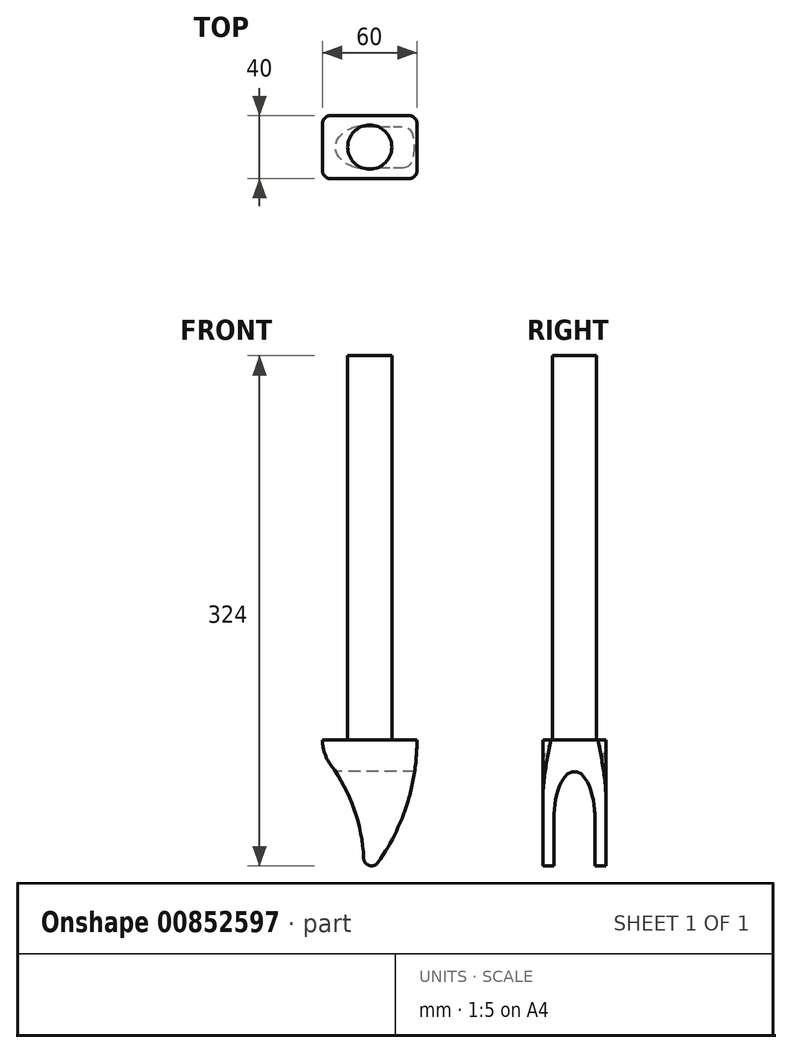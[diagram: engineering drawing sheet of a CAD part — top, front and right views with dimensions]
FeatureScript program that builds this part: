
annotation { "Feature Type Name" : "Feature", "Feature Type Description" : "" }
export const myFeature = defineFeature(function(context is Context, id is Id, definition is map)
    precondition{}
    {
        {
            var Q0;
            Q0=qCreatedBy(makeId("Top.planeOp"),FACE);
            var sketch = newSketch(context, id + "F0", { "sketchPlane" : qUnion([Q0])});
            skCircle(sketch, "E0", {"center": v(0, 0) * mm, "radius": 14 * mm});
            skSolve(sketch);
        }
        {
            var Q0;
            Q0=makeQuery(id+"F0.imprint","IMPRINT",FACE,{"disambiguationData":[TD([[makeQuery(id+"F0.imprint","IMPRINT",EDGE,{"derivedFrom":sQuery(id+"F0.wireOp",EDGE,"E0")}),1.0]])]});
            extrude(context, id + "F1", {"entities" : qUnion([Q0]), "depth" : 244 * mm, "offsetDistance" : 25 * mm});
        }
        {
            var Q0;
            Q0=qCreatedBy(makeId("Top.planeOp"),FACE);
            var sketch = newSketch(context, id + "F2", { "sketchPlane" : qUnion([Q0])});
            skLineSegment(sketch, "E1.bottom", {"start": v(-30, 20) * mm, "end": v(30, 20) * mm});
            skLineSegment(sketch, "E1.top", {"start": v(-30, -20) * mm, "end": v(30, -20) * mm});
            skLineSegment(sketch, "E1.left", {"start": v(-30, 20) * mm, "end": v(-30, -20) * mm});
            skLineSegment(sketch, "E1.right", {"start": v(30, 20) * mm, "end": v(30, -20) * mm});
            skPoint(sketch, "E1.middle", {"position": v(0, 0) * mm});
            skSolve(sketch);
        }
        {
            var Q0;
            Q0=makeQuery(id+"F2.imprint","IMPRINT",FACE,{"disambiguationData":[TD([[makeQuery(id+"F2.imprint","IMPRINT",EDGE,{"derivedFrom":sQuery(id+"F2.wireOp",EDGE,"E1.bottom")}),-1.0]])]});
            extrude(context, id + "F3", {"entities" : qUnion([Q0]), "operationType" : NewBodyOperationType.ADD, "oppositeDirection" : true, "depth" : 80 * mm, "offsetDistance" : 25 * mm});
        }
        {
            var Q0;
            Q0=makeQuery(id+"F3.opExtrude","SWEPT_EDGE",EDGE,{"disambiguationData":[OSD([sQuery(id+"F2.wireOp",EDGE,"E1.top"),sQuery(id+"F2.wireOp",EDGE,"E1.right")])]});
            var Q1;
            Q1=makeQuery(id+"F3.opExtrude","SWEPT_EDGE",EDGE,{"disambiguationData":[OSD([sQuery(id+"F2.wireOp",EDGE,"E1.top"),sQuery(id+"F2.wireOp",EDGE,"E1.left")])]});
            var Q2;
            Q2=makeQuery(id+"F3.opExtrude","SWEPT_EDGE",EDGE,{"disambiguationData":[OSD([sQuery(id+"F2.wireOp",EDGE,"E1.bottom"),sQuery(id+"F2.wireOp",EDGE,"E1.right")])]});
            var Q3;
            Q3=makeQuery(id+"F3.opExtrude","SWEPT_EDGE",EDGE,{"disambiguationData":[OSD([sQuery(id+"F2.wireOp",EDGE,"E1.bottom"),sQuery(id+"F2.wireOp",EDGE,"E1.left")])]});
            fillet(context, id + "F4", {"entities" : qUnion([Q0, Q1, Q2, Q3]), "radius" : 5 * mm, "tangentPropagation" : true, "allowEdgeOverflow" : false});
        }
        {
            var Q0;
            Q0=qCreatedBy(makeId("Front.planeOp"),FACE);
            var sketch = newSketch(context, id + "F5", { "sketchPlane" : qUnion([Q0])});
            skLineSegment(sketch, "E2.0", {"start": v(-30, -85) * mm, "end": v(-30, 0) * mm});
            skLineSegment(sketch, "E3.0", {"start": v(30, 0) * mm, "end": v(30, -85) * mm});
            skArc(sketch, "E4", {"start": v(-30, 0) * mm, "mid": v(-28.66, -8.38) * mm, "end": v(-24.77, -15.93) * mm});
            skArc(sketch, "E5", {"start": v(-3.81, -75.22) * mm, "mid": v(-9.88, -44.02) * mm, "end": v(-24.77, -15.93) * mm});
            skArc(sketch, "E6", {"start": v(-3.81, -75.22) * mm, "mid": v(-0.22, -79.8) * mm, "end": v(5.27, -77.88) * mm});
            skArc(sketch, "E7", {"start": v(5.27, -77.88) * mm, "mid": v(23.67, -40.86) * mm, "end": v(30, 0) * mm});
            skLineSegment(sketch, "E8.0", {"start": v(-30, -85) * mm, "end": v(30, -85) * mm});
            skPoint(sketch, "E9.orphan", {"position": v(30, -80) * mm});
            skPoint(sketch, "E10.orphan", {"position": v(-30, -80) * mm});
            skSolve(sketch);
        }
        {
            var Q0;
            Q0 = qSketchRegion(id + "F5", true);
            extrude(context, id + "F6", {"entities" : qUnion([Q0]), "operationType" : NewBodyOperationType.REMOVE, "endBound" : BoundingType.SYMMETRIC, "depth" : 80 * mm, "offsetDistance" : 25 * mm});
        }
        {
            var Q0;
            Q0=qCreatedBy(makeId("Right.planeOp"),FACE);
            var sketch = newSketch(context, id + "F7", { "sketchPlane" : qUnion([Q0])});
            skEllipticalArc(sketch, "E11", {});
            skLineSegment(sketch, "E12", {"start": v(13, -50) * mm, "end": v(13, -80) * mm});
            skLineSegment(sketch, "E13", {"start": v(-13, -50) * mm, "end": v(-13, -80) * mm});
            skLineSegment(sketch, "E14", {"start": v(-13, -80) * mm, "end": v(13, -80) * mm});
            skPoint(sketch, "E15", {"position": v(0, -20) * mm});
            const initialGuessF7  = {"E11": [0, -0.05, 0, -1, 0.03, 0.013, 1.5707963267948966, 4.71238898038469]};
            skSetInitialGuess(sketch, initialGuessF7);
            skSolve(sketch);
        }
        {
            var Q0;
            Q0 = qSketchRegion(id + "F7", true);
            extrude(context, id + "F8", {"entities" : qUnion([Q0]), "operationType" : NewBodyOperationType.REMOVE, "endBound" : BoundingType.SYMMETRIC, "oppositeDirection" : true, "depth" : 70 * mm, "offsetDistance" : 25 * mm});
        }
    });
